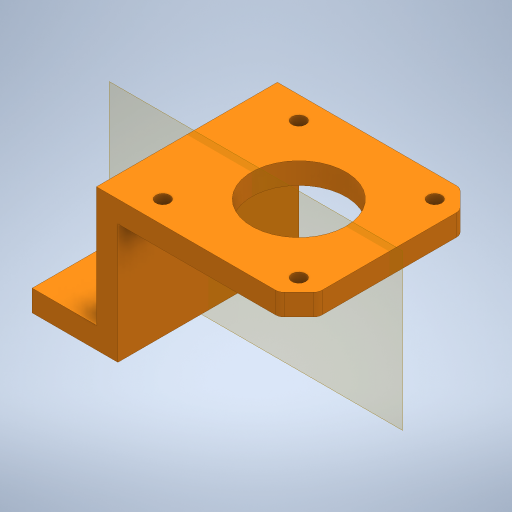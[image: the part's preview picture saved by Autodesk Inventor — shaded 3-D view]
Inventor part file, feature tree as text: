
AUTODESK INVENTOR PART (.ipt)
format: ipt  version: 2023 (Build 270158000, 158)  size: 301,056 bytes
history: native  units: mm
features: extrude x6, sketch x6, other x3, reference x2, plane x1
ambient origin geometry x8: Origin, YZ Plane, XZ Plane, XY Plane, X Axis, Y Axis, Z Axis, Center Point
bodies: Solid1 (feature_tree)
feature tree (18):
  extrude  "Extrusion1"  Depth=5.0mm TaperAngle=0.0deg
  extrude  "Extrusion2"  Depth=33.0mm
  extrude  "Extrusion3"  Depth=15.0mm TaperAngle=0.0deg
  extrude  "Extrusion4"  Depth=10.0mm
  extrude  "Extrusion5"  Depth=10.0mm
  plane  "Work Plane1"
  extrude  "Extrusion6"  Depth=10.0mm
  sketch  "Sketch1"  dims[d0=5.0mm d1=0.0mm d2=5.0mm d3=0.0mm]
  reference  "Reference1"
  reference  "Reference2"
  sketch  "Sketch2"  dims[d4=5.0mm d5=0.0mm d6=33.0mm]
  sketch  "Sketch3"  dims[d7=5.0mm d8=15.0mm d9=0.0mm]
  sketch  "Sketch4"  dims[d10=10.0mm d11=10.0mm]
  sketch  "Sketch5"  dims[d12=10.0mm d13=10.0mm]
  sketch  "Sketch6"  dims[d14=4.5mm d15=4.5mm d16=0.0mm d17=0.0mm d18=10.0mm d19=0.0mm]
  other  "<userpath>\OneDrive\Objet3D\3DPrinter\3DPrinterBeltCoreXY.iam"
  other  "3DPrinterBeltCoreXY.iam"
  other  "E3D Stepper Motor:4"
